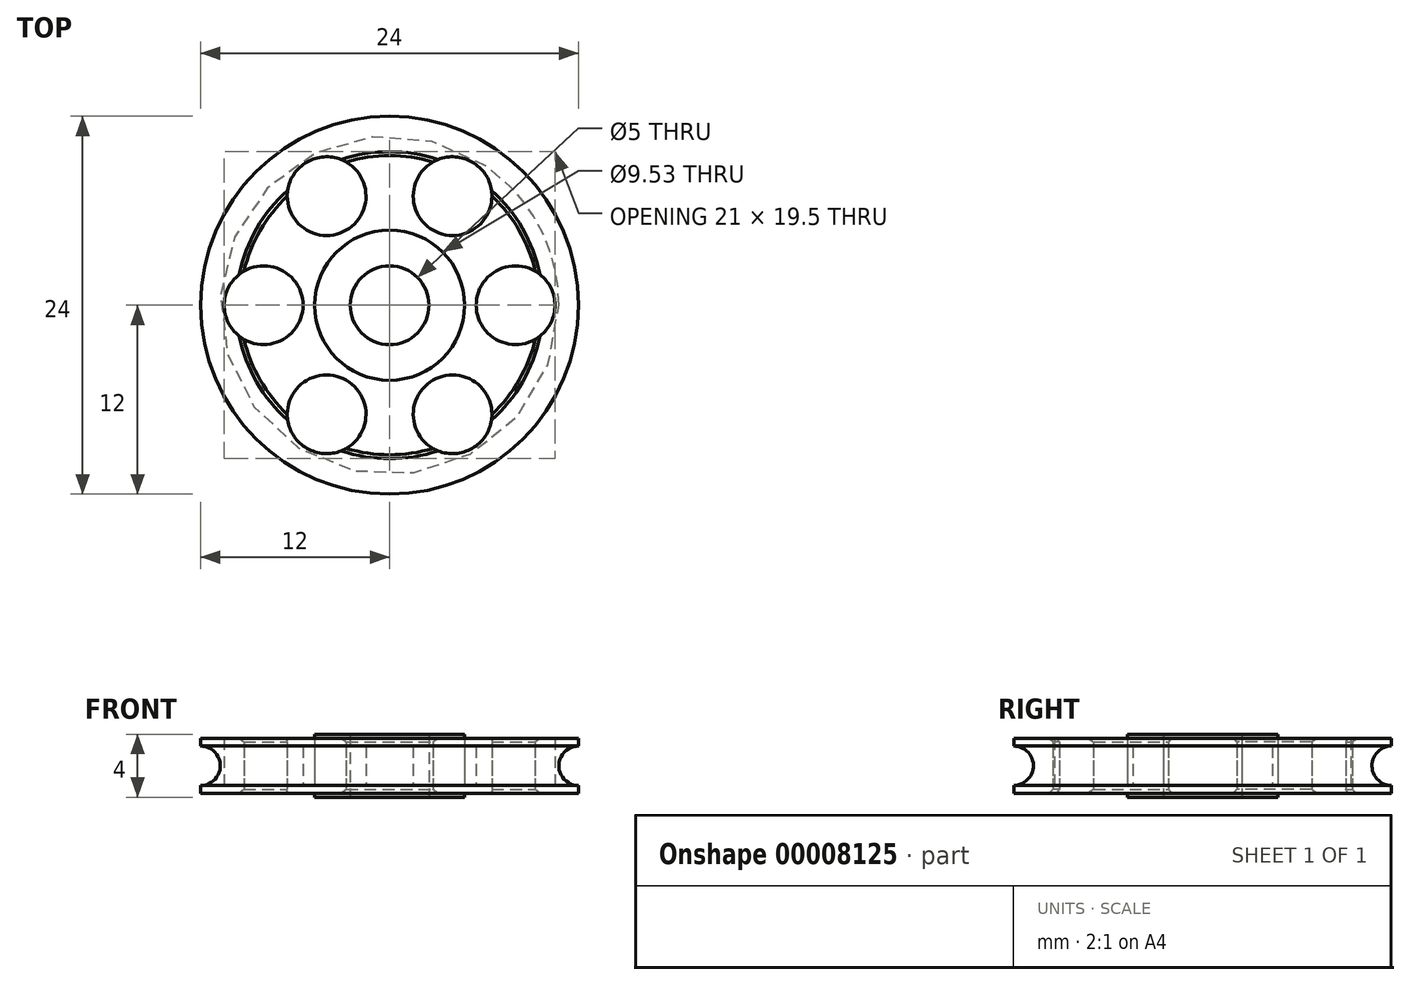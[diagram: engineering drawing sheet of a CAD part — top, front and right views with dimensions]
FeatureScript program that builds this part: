
annotation { "Feature Type Name" : "Feature", "Feature Type Description" : "" }
export const myFeature = defineFeature(function(context is Context, id is Id, definition is map)
    precondition{}
    {
        {
            var Q0;
            Q0=qCreatedBy(makeId("Top.planeOp"),FACE);
            var sketch = newSketch(context, id + "F0", { "sketchPlane" : qUnion([Q0])});
            skCircle(sketch, "E0", {"center": v(0, 0) * mm, "radius": 2.5 * mm});
            skCircle(sketch, "E1", {"center": v(0, 0) * mm, "radius": 4.77 * mm});
            skCircle(sketch, "E2", {"center": v(0, 0) * mm, "radius": 9.5 * mm});
            skCircle(sketch, "E3", {"center": v(0, 0) * mm, "radius": 12 * mm});
            skLineSegment(sketch, "E4", {"start": v(0, 0) * mm, "end": v(16.13, 0) * mm, "construction": true});
            skCircle(sketch, "E5", {"center": v(8, 0) * mm, "radius": 2.5 * mm});
            skCircle(sketch, "E6.1.0", {"center": v(4, 6.93) * mm, "radius": 2.5 * mm});
            skCircle(sketch, "E6.2.0", {"center": v(-4, 6.93) * mm, "radius": 2.5 * mm});
            skCircle(sketch, "E6.3.0", {"center": v(-8, 0) * mm, "radius": 2.5 * mm});
            skCircle(sketch, "E6.4.0", {"center": v(-4, -6.93) * mm, "radius": 2.5 * mm});
            skCircle(sketch, "E6.5.0", {"center": v(4, -6.93) * mm, "radius": 2.5 * mm});
            skSolve(sketch);
        }
        {
            var Q0;
            Q0 = qSketchRegion(id + "F0", true);
            extrude(context, id + "F1", {"entities" : qUnion([Q0]), "endBound" : BoundingType.SYMMETRIC, "depth" : 3.5 * mm});
        }
        {
            var Q0;
            Q0=makeQuery(id+"F0.imprint","IMPRINT",FACE,{"disambiguationData":[TD([[makeQuery(id+"F0.imprint","IMPRINT",EDGE,{"derivedFrom":sQuery(id+"F0.wireOp",EDGE,"E0")}),-1.0]])]});
            extrude(context, id + "F2", {"entities" : qUnion([Q0]), "endBound" : BoundingType.SYMMETRIC, "depth" : 4 * mm});
        }
        {
            var Q0;
            Q0=makeQuery(id+"F0.imprint","IMPRINT",FACE,{"disambiguationData":[TD([[makeQuery(id+"F0.imprint","IMPRINT",EDGE,{"derivedFrom":sQuery(id+"F0.wireOp",EDGE,"E1")}),-1.0]])]});
            extrude(context, id + "F3", {"entities" : qUnion([Q0]), "endBound" : BoundingType.SYMMETRIC, "depth" : 2.5 * mm});
        }
        {
            var Q0;
            {var subQ0=sQuery(id+"F0.wireOp",EDGE,"E2");Q0=makeQuery(id+"F1.opExtrude","CAP_EDGE",EDGE,{"disambiguationData":[OSD([subQ0]),TDD([makeQuery(id+"F0.imprint","IMPRINT",EDGE,{"disambiguationData":[TD([[makeQuery(id+"F0.imprint","INTERSECT",VERTEX,{"disambiguationData":[OD(1.0)],"derivedFrom":[subQ0,sQuery(id+"F0.wireOp",EDGE,"E6.2.0")]}),-1.0]])],"derivedFrom":subQ0})])],"isStart":false});}
            var Q1;
            {var subQ0=sQuery(id+"F0.wireOp",EDGE,"E2");Q1=makeQuery(id+"F1.opExtrude","CAP_EDGE",EDGE,{"disambiguationData":[OSD([subQ0]),TDD([makeQuery(id+"F0.imprint","IMPRINT",EDGE,{"disambiguationData":[TD([[makeQuery(id+"F0.imprint","INTERSECT",VERTEX,{"disambiguationData":[OD(1.0)],"derivedFrom":[subQ0,sQuery(id+"F0.wireOp",EDGE,"E6.1.0")]}),-1.0]])],"derivedFrom":subQ0})])],"isStart":false});}
            var Q2;
            {var subQ0=sQuery(id+"F0.wireOp",EDGE,"E2");Q2=makeQuery(id+"F1.opExtrude","CAP_EDGE",EDGE,{"disambiguationData":[OSD([subQ0]),TDD([makeQuery(id+"F0.imprint","IMPRINT",EDGE,{"disambiguationData":[TD([[makeQuery(id+"F0.imprint","INTERSECT",VERTEX,{"disambiguationData":[OD(1.0)],"derivedFrom":[subQ0,sQuery(id+"F0.wireOp",EDGE,"E6.3.0")]}),-1.0]])],"derivedFrom":subQ0})])],"isStart":false});}
            var Q3;
            {var subQ0=sQuery(id+"F0.wireOp",EDGE,"E2");Q3=makeQuery(id+"F1.opExtrude","CAP_EDGE",EDGE,{"disambiguationData":[OSD([subQ0]),TDD([makeQuery(id+"F0.imprint","IMPRINT",EDGE,{"disambiguationData":[TD([[makeQuery(id+"F0.imprint","INTERSECT",VERTEX,{"disambiguationData":[OD(1.0)],"derivedFrom":[subQ0,sQuery(id+"F0.wireOp",EDGE,"E6.4.0")]}),-1.0]])],"derivedFrom":subQ0})])],"isStart":false});}
            var Q4;
            {var subQ0=sQuery(id+"F0.wireOp",EDGE,"E2");Q4=makeQuery(id+"F1.opExtrude","CAP_EDGE",EDGE,{"disambiguationData":[OSD([subQ0]),TDD([makeQuery(id+"F0.imprint","IMPRINT",EDGE,{"disambiguationData":[TD([[makeQuery(id+"F0.imprint","INTERSECT",VERTEX,{"disambiguationData":[OD(1.0)],"derivedFrom":[subQ0,sQuery(id+"F0.wireOp",EDGE,"E6.5.0")]}),-1.0]])],"derivedFrom":subQ0})])],"isStart":false});}
            var Q5;
            {var subQ0=sQuery(id+"F0.wireOp",EDGE,"E2");Q5=makeQuery(id+"F1.opExtrude","CAP_EDGE",EDGE,{"disambiguationData":[OSD([subQ0]),TDD([makeQuery(id+"F0.imprint","IMPRINT",EDGE,{"disambiguationData":[TD([[makeQuery(id+"F0.imprint","INTERSECT",VERTEX,{"disambiguationData":[OD(0.0)],"derivedFrom":[subQ0,sQuery(id+"F0.wireOp",EDGE,"E6.1.0")]}),1.0]])],"derivedFrom":subQ0})])],"isStart":false});}
            chamfer(context, id + "F4", {"entities" : qUnion([Q0, Q1, Q2, Q3, Q4, Q5]), "width" : 0.25 * mm, "tangentPropagation" : true});
        }
        {
            var Q0;
            {var subQ0=sQuery(id+"F0.wireOp",EDGE,"E2");Q0=makeQuery(id+"F1.opExtrude","CAP_EDGE",EDGE,{"disambiguationData":[OSD([subQ0]),TDD([makeQuery(id+"F0.imprint","IMPRINT",EDGE,{"disambiguationData":[TD([[makeQuery(id+"F0.imprint","INTERSECT",VERTEX,{"disambiguationData":[OD(1.0)],"derivedFrom":[subQ0,sQuery(id+"F0.wireOp",EDGE,"E6.5.0")]}),-1.0]])],"derivedFrom":subQ0})])],"isStart":true});}
            var Q1;
            {var subQ0=sQuery(id+"F0.wireOp",EDGE,"E2");Q1=makeQuery(id+"F1.opExtrude","CAP_EDGE",EDGE,{"disambiguationData":[OSD([subQ0]),TDD([makeQuery(id+"F0.imprint","IMPRINT",EDGE,{"disambiguationData":[TD([[makeQuery(id+"F0.imprint","INTERSECT",VERTEX,{"disambiguationData":[OD(0.0)],"derivedFrom":[subQ0,sQuery(id+"F0.wireOp",EDGE,"E6.1.0")]}),1.0]])],"derivedFrom":subQ0})])],"isStart":true});}
            var Q2;
            {var subQ0=sQuery(id+"F0.wireOp",EDGE,"E2");Q2=makeQuery(id+"F1.opExtrude","CAP_EDGE",EDGE,{"disambiguationData":[OSD([subQ0]),TDD([makeQuery(id+"F0.imprint","IMPRINT",EDGE,{"disambiguationData":[TD([[makeQuery(id+"F0.imprint","INTERSECT",VERTEX,{"disambiguationData":[OD(1.0)],"derivedFrom":[subQ0,sQuery(id+"F0.wireOp",EDGE,"E6.4.0")]}),-1.0]])],"derivedFrom":subQ0})])],"isStart":true});}
            var Q3;
            {var subQ0=sQuery(id+"F0.wireOp",EDGE,"E2");Q3=makeQuery(id+"F1.opExtrude","CAP_EDGE",EDGE,{"disambiguationData":[OSD([subQ0]),TDD([makeQuery(id+"F0.imprint","IMPRINT",EDGE,{"disambiguationData":[TD([[makeQuery(id+"F0.imprint","INTERSECT",VERTEX,{"disambiguationData":[OD(1.0)],"derivedFrom":[subQ0,sQuery(id+"F0.wireOp",EDGE,"E6.3.0")]}),-1.0]])],"derivedFrom":subQ0})])],"isStart":true});}
            var Q4;
            {var subQ0=sQuery(id+"F0.wireOp",EDGE,"E2");Q4=makeQuery(id+"F1.opExtrude","CAP_EDGE",EDGE,{"disambiguationData":[OSD([subQ0]),TDD([makeQuery(id+"F0.imprint","IMPRINT",EDGE,{"disambiguationData":[TD([[makeQuery(id+"F0.imprint","INTERSECT",VERTEX,{"disambiguationData":[OD(1.0)],"derivedFrom":[subQ0,sQuery(id+"F0.wireOp",EDGE,"E6.2.0")]}),-1.0]])],"derivedFrom":subQ0})])],"isStart":true});}
            var Q5;
            {var subQ0=sQuery(id+"F0.wireOp",EDGE,"E2");Q5=makeQuery(id+"F1.opExtrude","CAP_EDGE",EDGE,{"disambiguationData":[OSD([subQ0]),TDD([makeQuery(id+"F0.imprint","IMPRINT",EDGE,{"disambiguationData":[TD([[makeQuery(id+"F0.imprint","INTERSECT",VERTEX,{"disambiguationData":[OD(1.0)],"derivedFrom":[subQ0,sQuery(id+"F0.wireOp",EDGE,"E6.1.0")]}),-1.0]])],"derivedFrom":subQ0})])],"isStart":true});}
            chamfer(context, id + "F5", {"entities" : qUnion([Q0, Q1, Q2, Q3, Q4, Q5]), "width" : 0.25 * mm, "tangentPropagation" : true});
        }
        {
            var Q0;
            Q0=qCreatedBy(makeId("Front.planeOp"),FACE);
            var sketch = newSketch(context, id + "F6", { "sketchPlane" : qUnion([Q0])});
            skCircle(sketch, "E7", {"center": v(12, 0) * mm, "radius": 1.25 * mm});
            skLineSegment(sketch, "E8", {"start": v(0, 0) * mm, "end": v(0, 11.92) * mm, "construction": true});
            skSolve(sketch);
        }
        {
            var Q0;
            Q0 = qSketchRegion(id + "F6", true);
            var Q1;
            Q1=sQuery(id+"F6.wireOp",EDGE,"E8");
            revolve(context, id + "F7", {"operationType" : NewBodyOperationType.REMOVE, "entities" : qUnion([Q0]), "axis" : qUnion([Q1]), "revolveType" : RevolveType.FULL, "oppositeDirection" : true});
        }
    });
